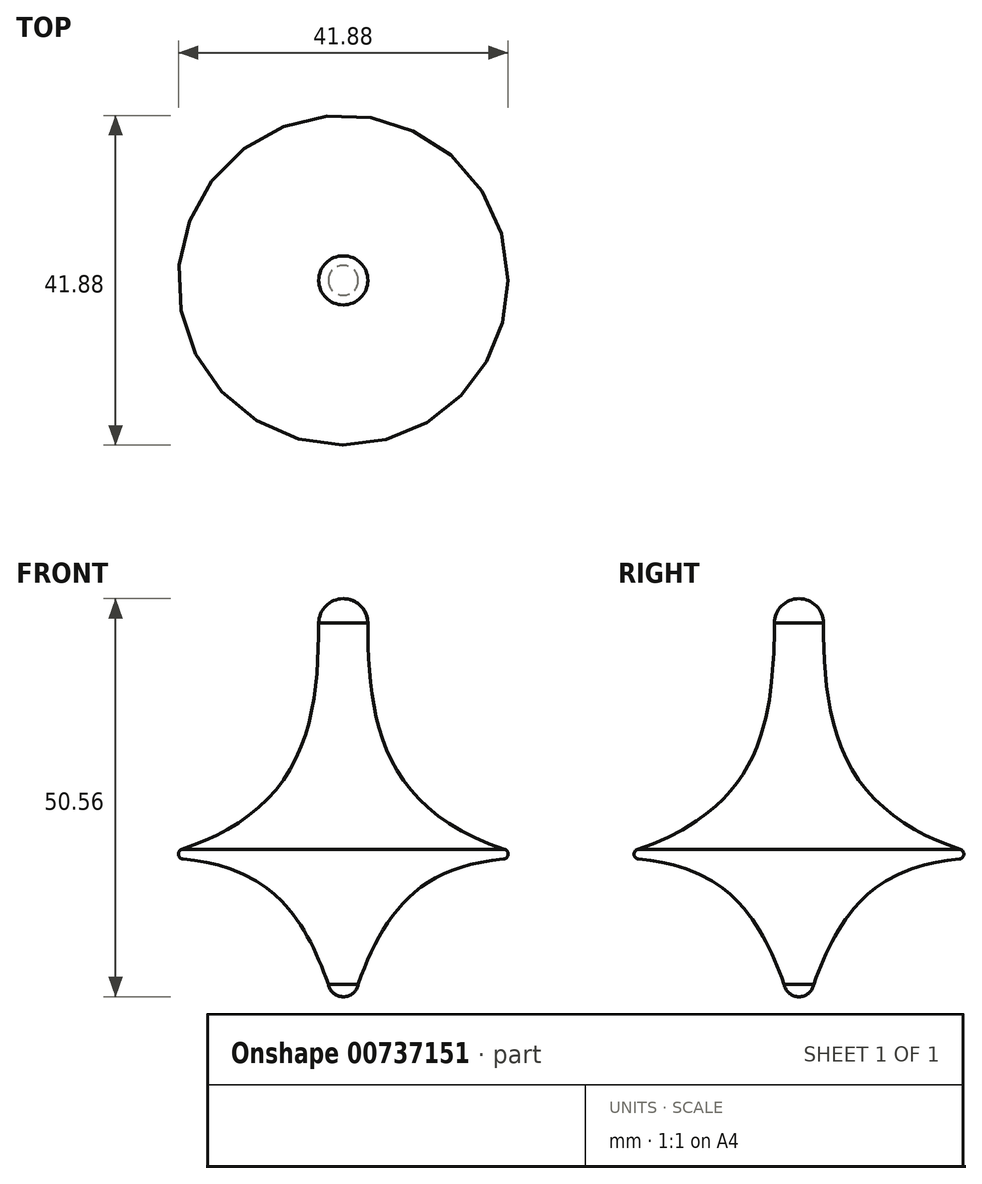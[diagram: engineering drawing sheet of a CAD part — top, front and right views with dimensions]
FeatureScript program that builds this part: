
annotation { "Feature Type Name" : "Feature", "Feature Type Description" : "" }
export const myFeature = defineFeature(function(context is Context, id is Id, definition is map)
    precondition{}
    {
        {
            var Q0;
            Q0=qCreatedBy(makeId("Front.planeOp"),FACE);
            var sketch = newSketch(context, id + "F0", { "sketchPlane" : qUnion([Q0])});
            skArc(sketch, "E0", {"start": v(3.11, 29.78) * mm, "mid": v(2.2, 31.98) * mm, "end": v(0, 32.9) * mm});
            skFitSpline(sketch, "E1", {"points": [v(3.11, 29.78) * mm, v(5.78, 13.07) * mm, v(24.3, 0) * mm], "startDerivative": vector(0.4, -36.49) * mm, "endDerivative": vector(57.9, -13.58) * mm});
            skArc(sketch, "E2", {"start": v(0, -17.66) * mm, "mid": v(1.24, -17.21) * mm, "end": v(1.9, -16.07) * mm});
            skFitSpline(sketch, "E3", {"points": [v(24.3, 0) * mm, v(8.03, -5.34) * mm, v(1.9, -16.07) * mm], "startDerivative": vector(-45.14, 0) * mm, "endDerivative": vector(-9.39, -26.5) * mm});
            skLineSegment(sketch, "E4", {"start": v(0, 32.9) * mm, "end": v(0, -17.66) * mm});
            skLineSegment(sketch, "E5", {"start": v(0, 45.41) * mm, "end": v(0, -22.24) * mm, "construction": true});
            skSolve(sketch);
        }
        {
            var Q0;
            Q0=makeQuery(id+"F0.imprint","IMPRINT",FACE,{"disambiguationData":[TD([[makeQuery(id+"F0.imprint","IMPRINT",EDGE,{"derivedFrom":sQuery(id+"F0.wireOp",EDGE,"E0")}),1.0]])]});
            var Q1;
            Q1=sQuery(id+"F0.wireOp",EDGE,"E5");
            revolve(context, id + "F1", {"surfaceOperationType" : NewSurfaceOperationType.NEW, "entities" : qUnion([Q0]), "axis" : qUnion([Q1]), "revolveType" : RevolveType.FULL});
        }
        {
            var Q0;
            Q0=makeQuery(id+"F1.opRevolve","SWEPT_EDGE",EDGE,{"disambiguationData":[OSD([sQuery(id+"F0.wireOp",EDGE,"E1"),sQuery(id+"F0.wireOp",EDGE,"E3")])]});
            fillet(context, id + "F2", {"entities" : qUnion([Q0]), "radius" : 0.64 * mm, "tangentPropagation" : true, "allowEdgeOverflow" : false});
        }
    });
